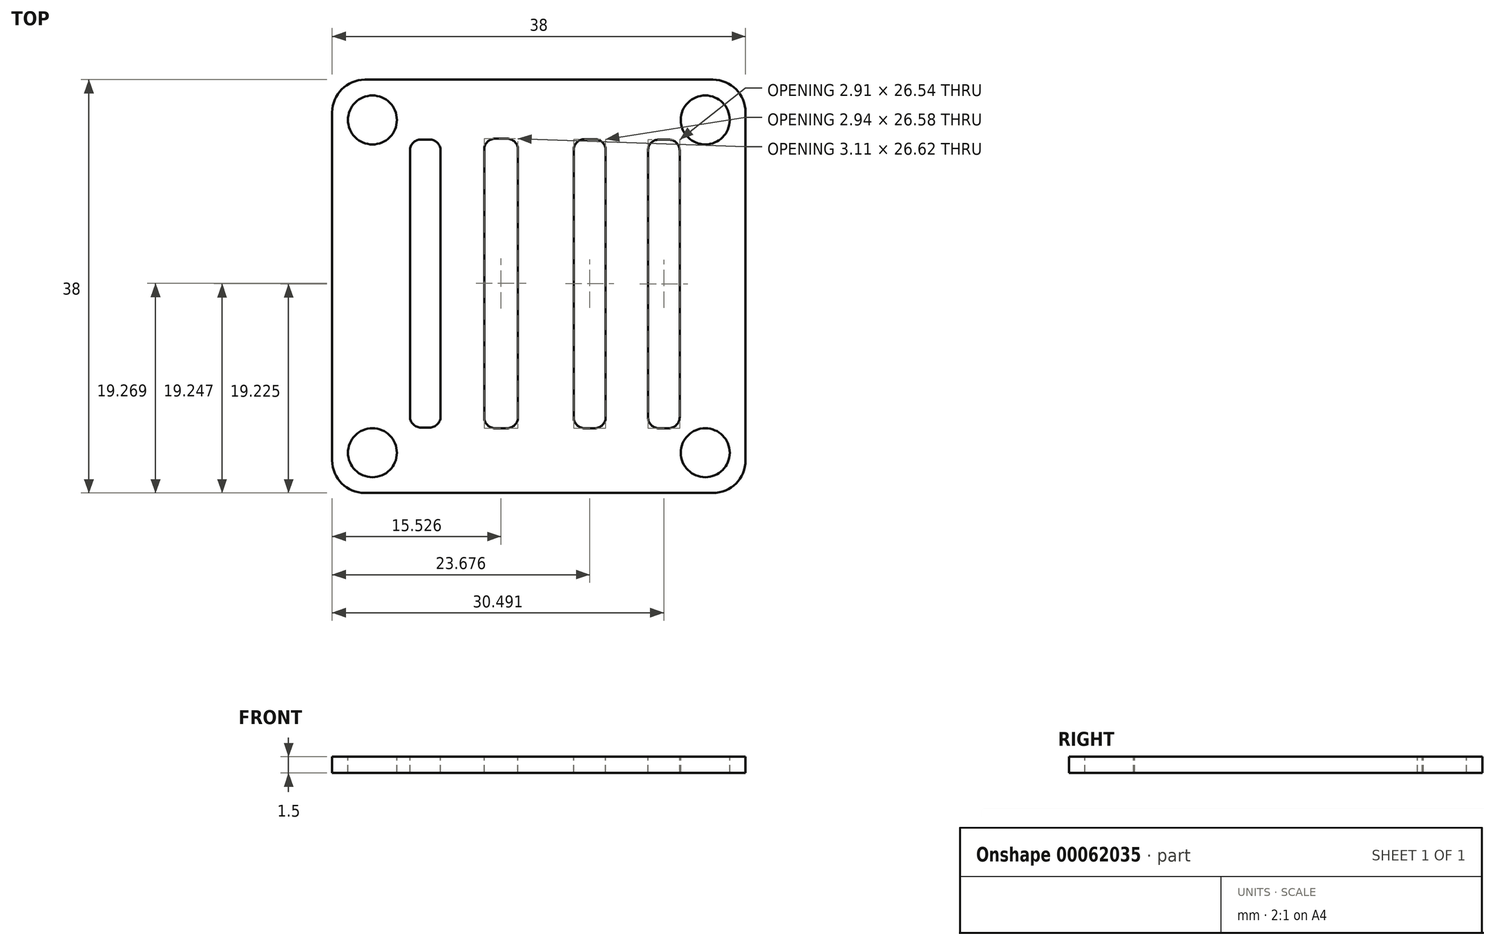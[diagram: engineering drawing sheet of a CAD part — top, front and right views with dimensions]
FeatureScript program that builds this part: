
annotation { "Feature Type Name" : "Feature", "Feature Type Description" : "" }
export const myFeature = defineFeature(function(context is Context, id is Id, definition is map)
    precondition{}
    {
        {
            var Q0;
            Q0=qCreatedBy(makeId("Top.planeOp"),FACE);
            var sketch = newSketch(context, id + "F0", { "sketchPlane" : qUnion([Q0])});
            skLineSegment(sketch, "E0.bottom", {"start": v(-43.1, 38) * mm, "end": v(-5.1, 38) * mm});
            skLineSegment(sketch, "E0.top", {"start": v(-43.1, 0) * mm, "end": v(-5.1, 0) * mm});
            skLineSegment(sketch, "E0.left", {"start": v(-43.1, 38) * mm, "end": v(-43.1, 0) * mm});
            skLineSegment(sketch, "E0.right", {"start": v(-5.1, 38) * mm, "end": v(-5.1, 0) * mm});
            skSolve(sketch);
        }
        {
            var Q0;
            Q0 = qSketchRegion(id + "F0", true);
            extrude(context, id + "F1", {"entities" : qUnion([Q0]), "depth" : 1.5 * mm});
        }
        {
            var Q0;
            Q0=makeQuery(id+"F1.opExtrude","CAP_FACE",FACE,{"disambiguationData":[OSD([sQuery(id+"F0.wireOp",EDGE,"E0.bottom"),sQuery(id+"F0.wireOp",EDGE,"E0.top"),sQuery(id+"F0.wireOp",EDGE,"E0.left"),sQuery(id+"F0.wireOp",EDGE,"E0.right")])],"isStart":false});
            var sketch = newSketch(context, id + "F2", { "sketchPlane" : qUnion([Q0])});
            skCircle(sketch, "E1", {"center": v(-39.4, 34.3) * mm, "radius": 2.25 * mm});
            skCircle(sketch, "E2", {"center": v(-8.8, 34.3) * mm, "radius": 2.25 * mm});
            skCircle(sketch, "E3", {"center": v(-8.8, 3.7) * mm, "radius": 2.25 * mm});
            skCircle(sketch, "E4", {"center": v(-39.4, 3.7) * mm, "radius": 2.25 * mm});
            skLineSegment(sketch, "E5.bottom", {"start": v(-35.96, 32.5) * mm, "end": v(-33.15, 32.5) * mm});
            skLineSegment(sketch, "E5.top", {"start": v(-35.96, 6.02) * mm, "end": v(-33.15, 6.02) * mm});
            skLineSegment(sketch, "E5.left", {"start": v(-35.96, 32.5) * mm, "end": v(-35.96, 6.02) * mm});
            skLineSegment(sketch, "E5.right", {"start": v(-33.15, 32.5) * mm, "end": v(-33.15, 6.02) * mm});
            skLineSegment(sketch, "E6.bottom", {"start": v(-29.14, 32.58) * mm, "end": v(-26.03, 32.58) * mm});
            skLineSegment(sketch, "E6.top", {"start": v(-29.14, 5.96) * mm, "end": v(-26.03, 5.96) * mm});
            skLineSegment(sketch, "E6.left", {"start": v(-29.14, 32.58) * mm, "end": v(-29.14, 5.96) * mm});
            skLineSegment(sketch, "E6.right", {"start": v(-26.03, 32.58) * mm, "end": v(-26.03, 5.96) * mm});
            skLineSegment(sketch, "E7.bottom", {"start": v(-20.9, 32.54) * mm, "end": v(-17.97, 32.54) * mm});
            skLineSegment(sketch, "E7.top", {"start": v(-20.9, 5.96) * mm, "end": v(-17.97, 5.96) * mm});
            skLineSegment(sketch, "E7.left", {"start": v(-20.9, 32.54) * mm, "end": v(-20.9, 5.96) * mm});
            skLineSegment(sketch, "E7.right", {"start": v(-17.97, 32.54) * mm, "end": v(-17.97, 5.96) * mm});
            skLineSegment(sketch, "E8.bottom", {"start": v(-14.08, 32.5) * mm, "end": v(-11.16, 32.5) * mm});
            skLineSegment(sketch, "E8.top", {"start": v(-14.08, 5.96) * mm, "end": v(-11.16, 5.96) * mm});
            skLineSegment(sketch, "E8.left", {"start": v(-14.08, 32.5) * mm, "end": v(-14.08, 5.96) * mm});
            skLineSegment(sketch, "E8.right", {"start": v(-11.16, 32.5) * mm, "end": v(-11.16, 5.96) * mm});
            skSolve(sketch);
        }
        {
            var Q0;
            Q0 = qSketchRegion(id + "F2", true);
            extrude(context, id + "F3", {"entities" : qUnion([Q0]), "operationType" : NewBodyOperationType.REMOVE, "endBound" : BoundingType.THROUGH_ALL, "oppositeDirection" : true, "depth" : 25 * mm});
        }
        {
            var Q0;
            Q0=makeQuery(id+"F1.opExtrude","SWEPT_EDGE",EDGE,{"disambiguationData":[OSD([sQuery(id+"F0.wireOp",EDGE,"E0.bottom"),sQuery(id+"F0.wireOp",EDGE,"E0.left")])]});
            var Q1;
            Q1=makeQuery(id+"F1.opExtrude","SWEPT_EDGE",EDGE,{"disambiguationData":[OSD([sQuery(id+"F0.wireOp",EDGE,"E0.bottom"),sQuery(id+"F0.wireOp",EDGE,"E0.right")])]});
            var Q2;
            Q2=makeQuery(id+"F1.opExtrude","SWEPT_EDGE",EDGE,{"disambiguationData":[OSD([sQuery(id+"F0.wireOp",EDGE,"E0.top"),sQuery(id+"F0.wireOp",EDGE,"E0.right")])]});
            var Q3;
            Q3=makeQuery(id+"F1.opExtrude","SWEPT_EDGE",EDGE,{"disambiguationData":[OSD([sQuery(id+"F0.wireOp",EDGE,"E0.top"),sQuery(id+"F0.wireOp",EDGE,"E0.left")])]});
            fillet(context, id + "F4", {"entities" : qUnion([Q0, Q1, Q2, Q3]), "radius" : 3 * mm, "tangentPropagation" : true, "allowEdgeOverflow" : false});
        }
        {
            var Q0;
            Q0=makeQuery(id+"F3.boolean.opBoolean","COPY",EDGE,{"derivedFrom":makeQuery(id+"F3.opExtrude","SWEPT_EDGE",EDGE,{"disambiguationData":[OSD([sQuery(id+"F2.wireOp",EDGE,"E5.bottom"),sQuery(id+"F2.wireOp",EDGE,"E5.left")])]})});
            var Q1;
            Q1=makeQuery(id+"F3.boolean.opBoolean","COPY",EDGE,{"derivedFrom":makeQuery(id+"F3.opExtrude","SWEPT_EDGE",EDGE,{"disambiguationData":[OSD([sQuery(id+"F2.wireOp",EDGE,"E5.top"),sQuery(id+"F2.wireOp",EDGE,"E5.left")])]})});
            var Q2;
            Q2=makeQuery(id+"F3.boolean.opBoolean","COPY",EDGE,{"derivedFrom":makeQuery(id+"F3.opExtrude","SWEPT_EDGE",EDGE,{"disambiguationData":[OSD([sQuery(id+"F2.wireOp",EDGE,"E6.top"),sQuery(id+"F2.wireOp",EDGE,"E6.left")])]})});
            var Q3;
            Q3=makeQuery(id+"F3.boolean.opBoolean","COPY",EDGE,{"derivedFrom":makeQuery(id+"F3.opExtrude","SWEPT_EDGE",EDGE,{"disambiguationData":[OSD([sQuery(id+"F2.wireOp",EDGE,"E7.top"),sQuery(id+"F2.wireOp",EDGE,"E7.left")])]})});
            var Q4;
            Q4=makeQuery(id+"F3.boolean.opBoolean","COPY",EDGE,{"derivedFrom":makeQuery(id+"F3.opExtrude","SWEPT_EDGE",EDGE,{"disambiguationData":[OSD([sQuery(id+"F2.wireOp",EDGE,"E8.top"),sQuery(id+"F2.wireOp",EDGE,"E8.left")])]})});
            var Q5;
            Q5=makeQuery(id+"F3.boolean.opBoolean","COPY",EDGE,{"derivedFrom":makeQuery(id+"F3.opExtrude","SWEPT_EDGE",EDGE,{"disambiguationData":[OSD([sQuery(id+"F2.wireOp",EDGE,"E8.top"),sQuery(id+"F2.wireOp",EDGE,"E8.right")])]})});
            var Q6;
            Q6=makeQuery(id+"F3.boolean.opBoolean","COPY",EDGE,{"derivedFrom":makeQuery(id+"F3.opExtrude","SWEPT_EDGE",EDGE,{"disambiguationData":[OSD([sQuery(id+"F2.wireOp",EDGE,"E7.top"),sQuery(id+"F2.wireOp",EDGE,"E7.right")])]})});
            var Q7;
            Q7=makeQuery(id+"F3.boolean.opBoolean","COPY",EDGE,{"derivedFrom":makeQuery(id+"F3.opExtrude","SWEPT_EDGE",EDGE,{"disambiguationData":[OSD([sQuery(id+"F2.wireOp",EDGE,"E6.top"),sQuery(id+"F2.wireOp",EDGE,"E6.right")])]})});
            var Q8;
            Q8=makeQuery(id+"F3.boolean.opBoolean","COPY",EDGE,{"derivedFrom":makeQuery(id+"F3.opExtrude","SWEPT_EDGE",EDGE,{"disambiguationData":[OSD([sQuery(id+"F2.wireOp",EDGE,"E5.top"),sQuery(id+"F2.wireOp",EDGE,"E5.right")])]})});
            var Q9;
            Q9=makeQuery(id+"F3.boolean.opBoolean","COPY",EDGE,{"derivedFrom":makeQuery(id+"F3.opExtrude","SWEPT_EDGE",EDGE,{"disambiguationData":[OSD([sQuery(id+"F2.wireOp",EDGE,"E8.bottom"),sQuery(id+"F2.wireOp",EDGE,"E8.right")])]})});
            var Q10;
            Q10=makeQuery(id+"F3.boolean.opBoolean","COPY",EDGE,{"derivedFrom":makeQuery(id+"F3.opExtrude","SWEPT_EDGE",EDGE,{"disambiguationData":[OSD([sQuery(id+"F2.wireOp",EDGE,"E7.bottom"),sQuery(id+"F2.wireOp",EDGE,"E7.right")])]})});
            var Q11;
            Q11=makeQuery(id+"F3.boolean.opBoolean","COPY",EDGE,{"derivedFrom":makeQuery(id+"F3.opExtrude","SWEPT_EDGE",EDGE,{"disambiguationData":[OSD([sQuery(id+"F2.wireOp",EDGE,"E6.bottom"),sQuery(id+"F2.wireOp",EDGE,"E6.right")])]})});
            var Q12;
            Q12=makeQuery(id+"F3.boolean.opBoolean","COPY",EDGE,{"derivedFrom":makeQuery(id+"F3.opExtrude","SWEPT_EDGE",EDGE,{"disambiguationData":[OSD([sQuery(id+"F2.wireOp",EDGE,"E5.bottom"),sQuery(id+"F2.wireOp",EDGE,"E5.right")])]})});
            var Q13;
            Q13=makeQuery(id+"F3.boolean.opBoolean","COPY",EDGE,{"derivedFrom":makeQuery(id+"F3.opExtrude","SWEPT_EDGE",EDGE,{"disambiguationData":[OSD([sQuery(id+"F2.wireOp",EDGE,"E6.bottom"),sQuery(id+"F2.wireOp",EDGE,"E6.left")])]})});
            var Q14;
            Q14=makeQuery(id+"F3.boolean.opBoolean","COPY",EDGE,{"derivedFrom":makeQuery(id+"F3.opExtrude","SWEPT_EDGE",EDGE,{"disambiguationData":[OSD([sQuery(id+"F2.wireOp",EDGE,"E7.bottom"),sQuery(id+"F2.wireOp",EDGE,"E7.left")])]})});
            var Q15;
            Q15=makeQuery(id+"F3.boolean.opBoolean","COPY",EDGE,{"derivedFrom":makeQuery(id+"F3.opExtrude","SWEPT_EDGE",EDGE,{"disambiguationData":[OSD([sQuery(id+"F2.wireOp",EDGE,"E8.bottom"),sQuery(id+"F2.wireOp",EDGE,"E8.left")])]})});
            fillet(context, id + "F5", {"entities" : qUnion([Q0, Q1, Q2, Q3, Q4, Q5, Q6, Q7, Q8, Q9, Q10, Q11, Q12, Q13, Q14, Q15]), "radius" : 1 * mm, "tangentPropagation" : true, "allowEdgeOverflow" : false});
        }
    });
